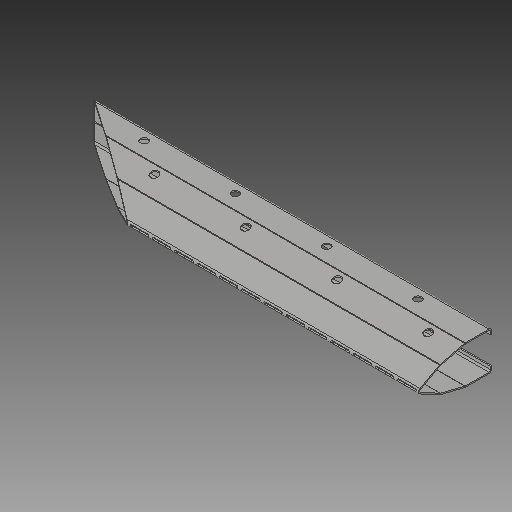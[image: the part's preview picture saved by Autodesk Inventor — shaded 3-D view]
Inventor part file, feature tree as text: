
AUTODESK INVENTOR PART (.ipt)
format: ipt  version: 2018 (Build 220112000, 112)  size: 822,784 bytes
history: native  units: mm
features: reference x24, other x21, sketch x14, sheet_metal_op x13, plane x9, projected_geometry x7, extrude x4
ambient origin geometry x8: Origin, YZ Plane, XZ Plane, XY Plane, X Axis, Y Axis, Z Axis, Center Point
bodies: Solid1 (feature_tree)
feature tree (92):
  parser-record x4  (decoder bookkeeping rows leaked as tree rows — omitted from the tree; the rows remain in map.json)
  plane  "Work Plane1"
  sheet_metal_op  "Face1"
  plane  "Work Plane2"
  sheet_metal_op  "Face2"
  plane  "Work Plane3"
  sheet_metal_op  "Face3"
  plane  "Work Plane4"
  sheet_metal_op  "Face4"
  plane  "Work Plane5"
  sheet_metal_op  "Face5"
  plane  "Work Plane6"
  sheet_metal_op  "Face6"
  plane  "Work Plane7"
  sheet_metal_op  "Face7"
  other  "midtplan"
  extrude  "Extrusion3"  Depth=5.0mm
  extrude  "hulsæt til stifter"  Depth=2.0mm
  plane  "Work Plane11"
  sketch  "Sketch13"  dims[d13=2.0mm]
  plane  "Work Plane12"
  extrude  "balusterhul"  Depth=5.0mm
  extrude  "balusterhul skråkompensering"  Depth=4.0mm
  sketch  "Sketch1"  dims[d0=4.0mm d1=5.0mm]
  reference  "Reference1"
  reference  "Reference2"
  reference  "Reference3"
  reference  "Reference4"
  other  "Plate1"
  sketch  "Sketch2"  dims[d2=4.0mm d3=2.0mm]
  reference  "Reference5"
  reference  "Reference6"
  reference  "Reference7"
  reference  "Reference8"
  other  "Plate2"
  sheet_metal_op  "Bend1"
  sketch  "Sketch3"  dims[d4=8.0mm d5=5.0mm]
  reference  "Reference9"
  reference  "Reference10"
  reference  "Reference11"
  other  "Plate3"
  sheet_metal_op  "Bend2"
  sketch  "Sketch4"  dims[d6=5.0mm d7=4.0mm]
  reference  "Reference12"
  reference  "Reference13"
  reference  "Reference14"
  reference  "Reference15"
  other  "Plate4"
  sheet_metal_op  "Bend3"
  sketch  "Sketch5"  dims[d8=2.0mm]
  reference  "Reference16"
  reference  "Reference17"
  reference  "Reference18"
  other  "Plate5"
  sheet_metal_op  "Bend4"
  sketch  "Sketch6"  dims[d9=8.0mm]
  reference  "Reference19"
  reference  "Reference20"
  reference  "Reference21"
  other  "Plate6"
  sheet_metal_op  "Bend5"
  sketch  "Sketch7"  dims[d10=5.0mm]
  reference  "Reference22"
  reference  "Reference23"
  other  "Plate7"
  sheet_metal_op  "Bend6"
  sketch  "Sketch8"  dims[d11=5.0mm]
  reference  "Reference24"
  projected_geometry  "Projected Loop1"
  other  "huller til stifter"
  projected_geometry  "Projected Loop3"
  sketch  "Sketch12"  dims[d12=4.0mm]
  projected_geometry  "Projected Loop4"
  sketch  "Sketch14"  dims[d14=8.0mm]
  sketch  "Sketch15"  dims[d15=5.0mm]
  projected_geometry  "Projected Loop5"
  projected_geometry  "Projected Loop6"
  sketch  "Sketch16"  dims[d16=5.0mm]
  projected_geometry  "Projected Loop7"
  projected_geometry  "Projected Loop8"
  sketch  "Sketch17"  dims[d17=4.0mm d18=2.0mm d19=8.0mm d20=5.0mm d21=5.0mm d22=4.0mm d23=2.0mm d24=8.0mm d25=5.0mm d26=5.0mm d27=4.0mm d28=2.0mm d29=8.0mm d30=5.0mm d31=4.0mm d32=0.0mm d33=3.0mm d39=250.0mm d41=33.7mm d42=33.7mm d43=60.0mm d44=60.0mm d45=16.85mm d46=65.0mm d47=60.0mm d48=10.0mm d49=0.0mm d69=10.0mm d70=0.0mm d73=96.672mm d75=5.986479mm d76=180.0mm d77=26.6mm d78=25.8mm d79=40.0mm d81=302.737mm d82=10.0mm d84=10.0mm d86=90.0deg d87=113.655385mm d88=56.827692mm d89=90.0deg d90=49.0mm d91=100.0mm d92=0.0mm d95=100.0mm d96=0.0mm d97=2.728615mm d99=1.364307mm d100=90.0mm d101=30.0mm d102=30.0mm d103=342.765mm d104=342.765mm d105=30.0mm d106=342.765mm d107=10.0mm d108=4.0mm d109=0.0mm d110=8.0mm d111=6.0mm d112=61.6mm d113=140.0mm d115=73.92mm d116=10.0mm d118=10.0mm d120=4.0mm d121=0.0mm]
  other  "Cut1"
  other  "plantehuller"
  other  "bukkeperforering"
  other  "modul bund.iam"
  other  "model:1"
  other  "Definition1"
  other  "modul.iam"
  other  "modul top.iam"
note: 4 file-system paths scrubbed to <path> (originals preserved in map.json)
